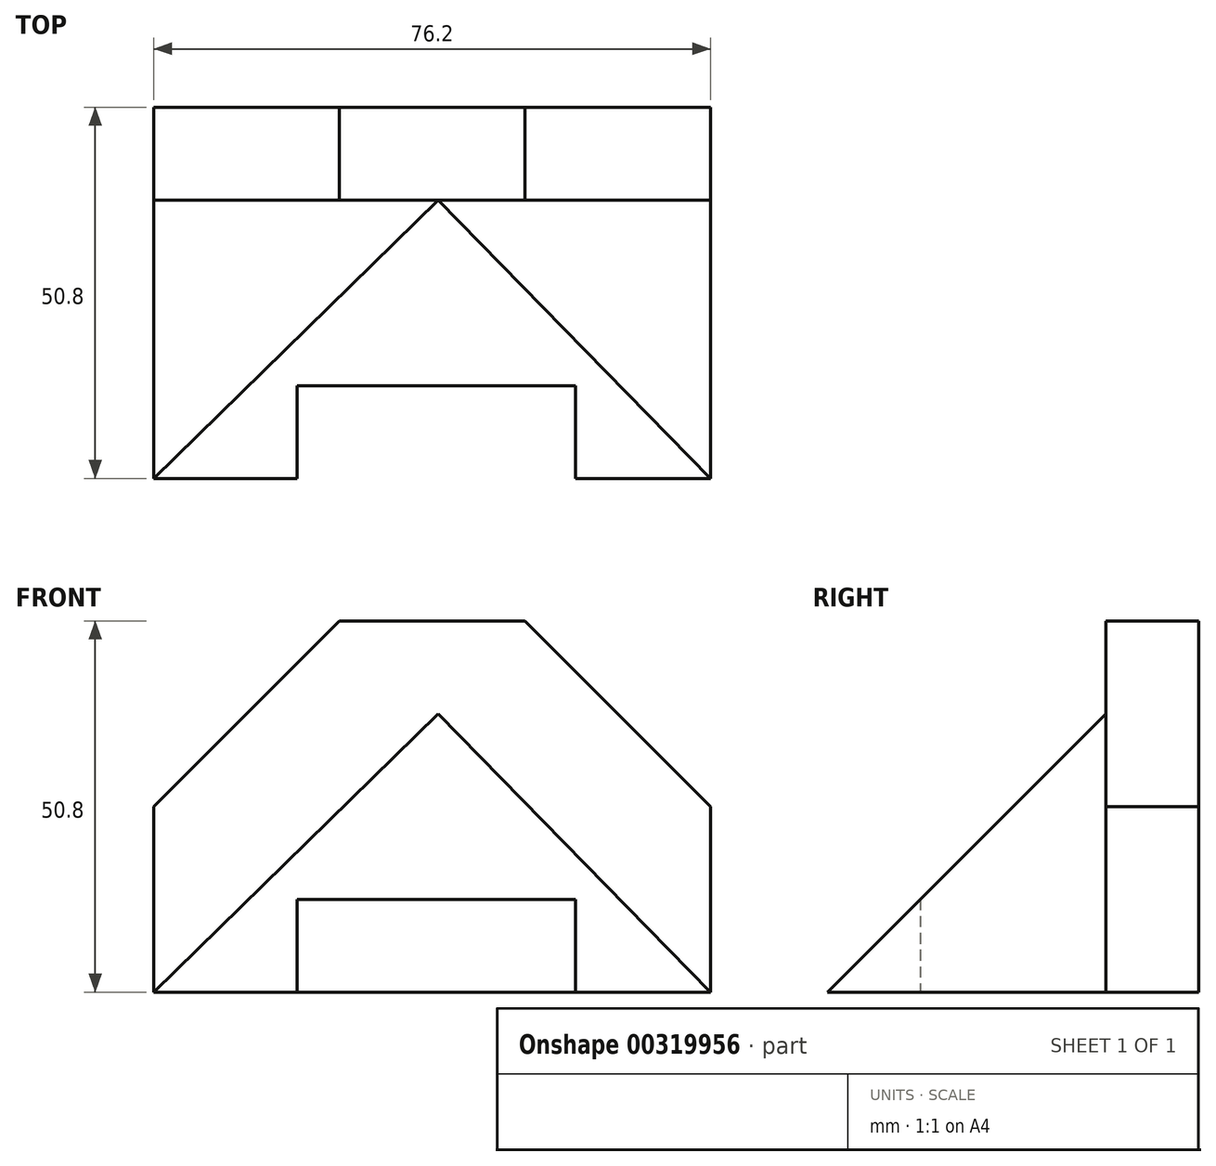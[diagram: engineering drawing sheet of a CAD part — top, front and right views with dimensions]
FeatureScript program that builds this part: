
annotation { "Feature Type Name" : "Feature", "Feature Type Description" : "" }
export const myFeature = defineFeature(function(context is Context, id is Id, definition is map)
    precondition{}
    {
        {
            var Q0;
            Q0=qCreatedBy(makeId("Front.planeOp"),FACE);
            var sketch = newSketch(context, id + "F0", { "sketchPlane" : qUnion([Q0])});
            skLineSegment(sketch, "E0", {"start": v(-38.93, 0) * mm, "end": v(-38.93, 25.4) * mm});
            skLineSegment(sketch, "E1", {"start": v(-38.93, 25.4) * mm, "end": v(-13.53, 50.8) * mm});
            skLineSegment(sketch, "E2", {"start": v(37.27, 0) * mm, "end": v(37.27, 25.4) * mm});
            skLineSegment(sketch, "E3", {"start": v(37.27, 25.4) * mm, "end": v(11.87, 50.8) * mm});
            skLineSegment(sketch, "E4", {"start": v(11.87, 50.8) * mm, "end": v(-13.53, 50.8) * mm});
            skLineSegment(sketch, "E5", {"start": v(-38.93, 0) * mm, "end": v(37.27, 0) * mm});
            skSolve(sketch);
        }
        {
            var Q0;
            Q0 = qSketchRegion(id + "F0", true);
            extrude(context, id + "F1", {"entities" : qUnion([Q0]), "endBound" : BoundingType.SYMMETRIC, "depth" : 12.7 * mm});
        }
        {
            var Q0;
            Q0=makeQuery(id+"F1.opExtrude","CAP_FACE",FACE,{"disambiguationData":[OSD([sQuery(id+"F0.wireOp",EDGE,"E0"),sQuery(id+"F0.wireOp",EDGE,"E1"),sQuery(id+"F0.wireOp",EDGE,"E2"),sQuery(id+"F0.wireOp",EDGE,"E3"),sQuery(id+"F0.wireOp",EDGE,"E4"),sQuery(id+"F0.wireOp",EDGE,"E5")])],"isStart":false});
            var sketch = newSketch(context, id + "F2", { "sketchPlane" : qUnion([Q0])});
            skLineSegment(sketch, "E6", {"start": v(-38.93, 0) * mm, "end": v(0, 38.1) * mm});
            skLineSegment(sketch, "E7", {"start": v(0, 38.1) * mm, "end": v(37.27, 0) * mm});
            skLineSegment(sketch, "E8", {"start": v(37.27, 0) * mm, "end": v(-38.93, 0) * mm});
            skSolve(sketch);
        }
        {
            var Q0;
            Q0 = qSketchRegion(id + "F2", true);
            extrude(context, id + "F3", {"entities" : qUnion([Q0]), "operationType" : NewBodyOperationType.ADD, "depth" : 38.1 * mm});
        }
        {
            var Q0;
            Q0=makeQuery(id+"F1.opExtrude","SWEPT_FACE",FACE,{"disambiguationData":[OSD([sQuery(id+"F0.wireOp",EDGE,"E2")])]});
            var sketch = newSketch(context, id + "F4", { "sketchPlane" : qUnion([Q0])});
            skLineSegment(sketch, "E9.0.0", {"start": v(-6.35, 0) * mm, "end": v(-6.35, 38.1) * mm});
            skLineSegment(sketch, "E9.0.1", {"start": v(-6.35, 38.1) * mm, "end": v(-44.45, 38.1) * mm});
            skLineSegment(sketch, "E9.0.2", {"start": v(-44.45, 38.1) * mm, "end": v(-44.45, 0) * mm});
            skLineSegment(sketch, "E9.0.3", {"start": v(-44.45, 0) * mm, "end": v(-6.35, 0) * mm});
            skLineSegment(sketch, "E10", {"start": v(-44.45, 0) * mm, "end": v(-6.35, 38.1) * mm});
            skSolve(sketch);
        }
        {
            var Q0;
            Q0=makeQuery(id+"F4.imprint","IMPRINT",FACE,{"disambiguationData":[TD([[makeQuery(id+"F4.imprint","IMPRINT",EDGE,{"derivedFrom":sQuery(id+"F4.wireOp",EDGE,"E9.0.2")}),1.0]])]});
            extrude(context, id + "F5", {"entities" : qUnion([Q0]), "operationType" : NewBodyOperationType.REMOVE, "oppositeDirection" : true, "depth" : 76.2 * mm});
        }
        {
            var Q0;
            Q0=makeQuery(id+"F3.boolean.opBoolean","MERGE",FACE,{"derivedFrom":[makeQuery(id+"F1.opExtrude","SWEPT_FACE",FACE,{"disambiguationData":[OSD([sQuery(id+"F0.wireOp",EDGE,"E5")])]}),makeQuery(id+"F3.opExtrude","SWEPT_FACE",FACE,{"disambiguationData":[OSD([sQuery(id+"F2.wireOp",EDGE,"E8")])]})]});
            var sketch = newSketch(context, id + "F6", { "sketchPlane" : qUnion([Q0])});
            skLineSegment(sketch, "E11", {"start": v(-19.34, 31.75) * mm, "end": v(-19.34, 44.45) * mm});
            skLineSegment(sketch, "E12", {"start": v(-19.34, 44.45) * mm, "end": v(18.76, 44.45) * mm});
            skLineSegment(sketch, "E13", {"start": v(-19.34, 31.75) * mm, "end": v(18.76, 31.75) * mm});
            skLineSegment(sketch, "E14", {"start": v(18.76, 31.75) * mm, "end": v(18.76, 44.45) * mm});
            skSolve(sketch);
        }
        {
            var Q0;
            Q0 = qSketchRegion(id + "F6", true);
            extrude(context, id + "F7", {"entities" : qUnion([Q0]), "operationType" : NewBodyOperationType.REMOVE, "oppositeDirection" : true, "depth" : 25.4 * mm});
        }
    });
